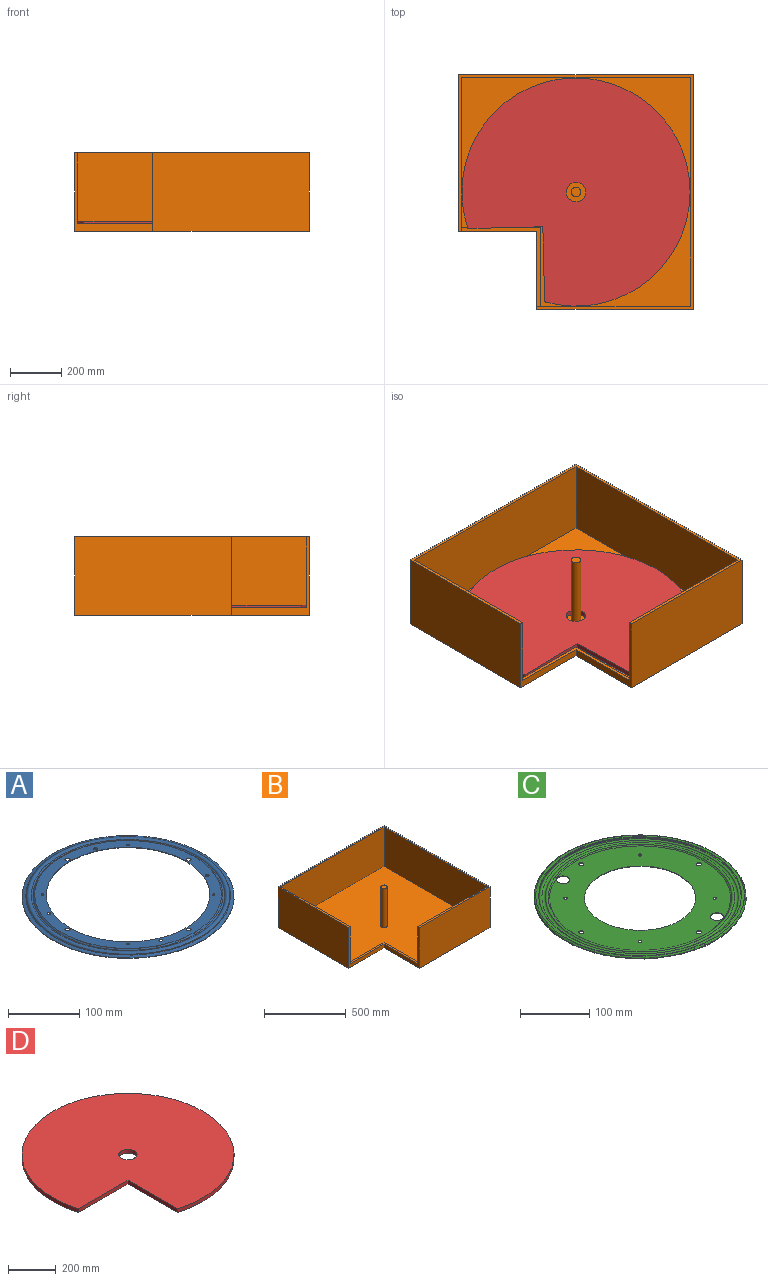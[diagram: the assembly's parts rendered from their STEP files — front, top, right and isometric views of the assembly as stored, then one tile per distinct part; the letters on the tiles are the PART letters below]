
ASSEMBLY  parts=4 mates=2
PART A: 26 faces, bbox 311.8x311.8x5.9 mm
  f0: cone r=143.42mm half-angle=74.7deg, axis (0,0,-1), area 5014.4mm2, adj f1,f13
  f1: cone r=148.89mm half-angle=15.3deg, axis (0,0,1), area 712.4mm2, adj f0,f2
  f2: cone r=143.62mm half-angle=74.7deg, axis (0,0,-1), area 5021.3mm2, adj f1,f3
  f3: torus R=144.02mm, axis (0,0,1), area 1025.9mm2, adj f2,f4
  f4: torus R=139.35mm, axis (0,0,1), area 6899.6mm2, adj f3,f5
  f5: torus R=134.68mm, axis (0,0,1), area 2728.8mm2, adj f4,f6
  f6: torus R=128.55mm, axis (0,0,1), area 2300.6mm2, adj f5,f7
  f7: plane 262.43x262.43mm, normal (0,0,1), area 12337.9mm2, adj f6,f8,f14,f15,f16,f17,f18,f19
  f8: cylinder r=114.9mm len=229.79mm, axis (0,0,1), area 550.1mm2, adj f7,f9
  f9: plane 262.05x262.05mm, normal (0,0,-1), area 12184mm2, adj f8,f10,f14,f15,f16,f17,f18,f19
  f10: torus R=128.55mm, axis (0,0,1), area 1854.7mm2, adj f9,f11
  f11: torus R=134.68mm, axis (0,0,1), area 3951.7mm2, adj f10,f12
  f12: torus R=139.35mm, axis (0,0,1), area 5576.4mm2, adj f11,f13
  f13: torus R=144.02mm, axis (0,0,1), area 1534.1mm2, adj f0,f12
  f14: cylinder r=3.57mm len=7.14mm, axis (0,0,1), area 17.1mm2, adj f7,f9
  f15: cylinder r=2.58mm len=5.16mm, axis (0,0,1), area 12.3mm2, adj f7,f9
  f16: cylinder r=1.65mm len=3.3mm, axis (0,0,1), area 7.9mm2, adj f7,f9
  f17: cylinder r=3.57mm len=7.14mm, axis (0,0,1), area 17.1mm2, adj f7,f9
  f18: cylinder r=2.58mm len=5.16mm, axis (0,0,1), area 12.3mm2, adj f7,f9
  f19: cylinder r=1.65mm len=3.3mm, axis (0,0,1), area 7.9mm2, adj f7,f9
  f20: cylinder r=3.57mm len=7.14mm, axis (0,0,1), area 17.1mm2, adj f7,f9
  f21: cylinder r=2.58mm len=5.16mm, axis (0,0,1), area 12.3mm2, adj f7,f9
  f22: cylinder r=1.65mm len=3.3mm, axis (0,0,1), area 7.9mm2, adj f7,f9
  f23: cylinder r=3.57mm len=7.14mm, axis (0,0,1), area 17.1mm2, adj f7,f9
  f24: cylinder r=2.58mm len=5.16mm, axis (0,0,1), area 12.3mm2, adj f7,f9
  f25: cylinder r=1.65mm len=3.3mm, axis (0,0,1), area 7.9mm2, adj f7,f9
PART B: 18 faces, bbox 914.4x914.4x304.8 mm
  f0: plane 914.4x914.4mm, normal (0,0,1), area 38225.7mm2, adj f1,f3,f4,f5,f6,f7,f10,f11
  f1: plane 304.8x304.8mm, normal (-1,0,0), area 12217.7mm2, adj f0,f3,f4,f8,f10,f15
  f2: plane 304.8x15.88mm, normal (0,1,0), area 4838.7mm2, adj f9,f13,f14,f15
  f3: plane 304.8x304.8mm, normal (0,-1,0), area 12217.7mm2, adj f0,f1,f7,f8,f13,f15
  f4: plane 609.6x304.8mm, normal (0,-1,0), area 185806.1mm2, adj f0,f1,f5,f8
  f5: plane 914.4x304.8mm, normal (1,0,0), area 278709.1mm2, adj f0,f4,f6,f8
  f6: plane 914.4x304.8mm, normal (0,1,0), area 278709.1mm2, adj f0,f5,f7,f8
  f7: plane 609.6x304.8mm, normal (-1,0,0), area 185806.1mm2, adj f0,f3,f6,f8
  f8: plane 914.4x914.4mm, normal (0,0,-1), area 743224.3mm2, adj f1,f3,f4,f5,f6,f7
  f9: plane 304.8x15.88mm, normal (1,0,0), area 4838.7mm2, adj f2,f10,f14,f15
  f10: plane 596.9x292.1mm, normal (0,1,0), area 174152.9mm2, adj f0,f1,f9,f11,f14,f15
  f11: plane 889x292.1mm, normal (-1,0,0), area 259676.9mm2, adj f0,f10,f12,f14
  f12: plane 889x292.1mm, normal (0,-1,0), area 259676.9mm2, adj f0,f11,f13,f14
  f13: plane 596.9x292.1mm, normal (1,0,0), area 174152.9mm2, adj f0,f2,f3,f12,f14,f15
  f14: plane 889x889mm, normal (0,0,1), area 696277.9mm2, adj f2,f9,f10,f11,f12,f13,f17
  f15: plane 304.8x304.8mm, normal (0,0,1), area 7580.6mm2, adj f1,f2,f3,f9,f10,f13
  f16: plane 38.1x38.1mm, normal (0,0,1), area 1140.1mm2, adj f17
  f17: cylinder r=19.05mm len=292.1mm, axis (0,0,-1), area 34962.8mm2, adj f14,f16
PART C: 31 faces, bbox 331.6x331.6x6.3 mm
  f0: torus R=150.41mm, axis (0,0,1), area 4196.6mm2, adj f19,f20
  f1: cone r=150.84mm half-angle=85.5deg, axis (0,0,-1), area 4152.8mm2, adj f2,f20
  f2: cone r=146.35mm half-angle=4.5deg, axis (0,0,1), area 700.8mm2, adj f1,f3
  f3: cone r=150.75mm half-angle=85.5deg, axis (0,0,-1), area 4120.6mm2, adj f2,f4
  f4: torus R=150.41mm, axis (0,0,1), area 5757.6mm2, adj f3,f5
  f5: plane 300.81x300.81mm, normal (0,0,1), area 2336.9mm2, adj f4,f6
  f6: torus R=148.81mm, axis (0,0,1), area 2165.2mm2, adj f5,f7
  f7: torus R=143.99mm, axis (0,0,1), area 4313.5mm2, adj f6,f8
  f8: torus R=139.35mm, axis (0,0,1), area 5466.4mm2, adj f7,f9
  f9: torus R=134.66mm, axis (0,0,1), area 3864.8mm2, adj f8,f10
  f10: torus R=128.78mm, axis (0,0,1), area 2048.8mm2, adj f9,f11
  f11: plane 261.49x261.49mm, normal (0,0,1), area 32588.1mm2, adj f10,f12,f21,f22,f23,f24,f25,f26
  f12: cylinder r=80.39mm len=160.78mm, axis (0,0,1), area 384.9mm2, adj f11,f13
  f13: plane 261.8x261.8mm, normal (0,0,-1), area 32711.9mm2, adj f12,f14,f21,f22,f23,f24,f25,f26
  f14: torus R=128.78mm, axis (0,0,1), area 2503.1mm2, adj f13,f15
  f15: torus R=134.66mm, axis (0,0,1), area 2671.3mm2, adj f14,f16
  f16: torus R=139.35mm, axis (0,0,1), area 6734.2mm2, adj f15,f17
  f17: torus R=143.99mm, axis (0,0,1), area 2993.9mm2, adj f16,f18
  f18: torus R=148.81mm, axis (0,0,1), area 2745.8mm2, adj f17,f19
  f19: plane 300.81x300.81mm, normal (0,0,-1), area 2427.4mm2, adj f0,f18
  f20: torus R=150.41mm, axis (0,0,1), area 3782.4mm2, adj f0,f1
  f21: cylinder r=2.58mm len=5.16mm, axis (0,0,1), area 12.3mm2, adj f11,f13
  f22: cylinder r=2.58mm len=5.16mm, axis (0,0,1), area 12.3mm2, adj f11,f13
  f23: cylinder r=2.58mm len=5.16mm, axis (0,0,1), area 12.3mm2, adj f11,f13
  f24: cylinder r=2.58mm len=5.16mm, axis (0,0,1), area 12.3mm2, adj f11,f13
  f25: cylinder r=9.53mm len=19.05mm, axis (0,0,1), area 45.6mm2, adj f11,f13
  f26: cylinder r=9.53mm len=19.05mm, axis (0,0,1), area 45.6mm2, adj f11,f13
  f27: cylinder r=3.57mm len=7.14mm, axis (0,0,1), area 17.1mm2, adj f11,f13
  f28: cylinder r=3.57mm len=7.14mm, axis (0,0,1), area 17.1mm2, adj f11,f13
  f29: cylinder r=3.57mm len=7.14mm, axis (0,0,1), area 17.1mm2, adj f11,f13
  f30: cylinder r=3.57mm len=7.14mm, axis (0,0,1), area 17.1mm2, adj f11,f13
PART D: 6 faces, bbox 889x889x19.1 mm
  f0: plane 292.1x19.05mm, normal (-1,0,0), area 5564.5mm2, adj f1,f2,f3,f4
  f1: cylinder r=444.5mm len=889mm, axis (0,0,-1), area 45020mm2, adj f0,f2,f3,f4
  f2: plane 292.1x19.05mm, normal (0,-1,0), area 5564.5mm2, adj f0,f1,f3,f4
  f3: plane 889x889mm, normal (0,0,1), area 559308mm2, adj f0,f1,f2,f5
  f4: plane 889x889mm, normal (0,0,-1), area 559308mm2, adj f0,f1,f2,f5
  f5: cylinder r=38.1mm len=76.2mm, axis (0,0,1), area 4560.4mm2, adj f3,f4
PLACE A t=(0,0,-3.14)mm
PLACE B t=(-152.4,-152.4,-19.05)mm fixed
PLACE C t=(0,0,-3.14)mm
PLACE D rot(axis=(0,0,1),1.3deg) t=(-148.8,-155.92,-621.46)mm
MATE revolute A.f0 <-> D.f1  axis (0,0,1) through (0,0,0.84)mm
MATE revolute C.f0 <-> B.f17  axis (0,0,1) through (0,0,-6.35)mm
